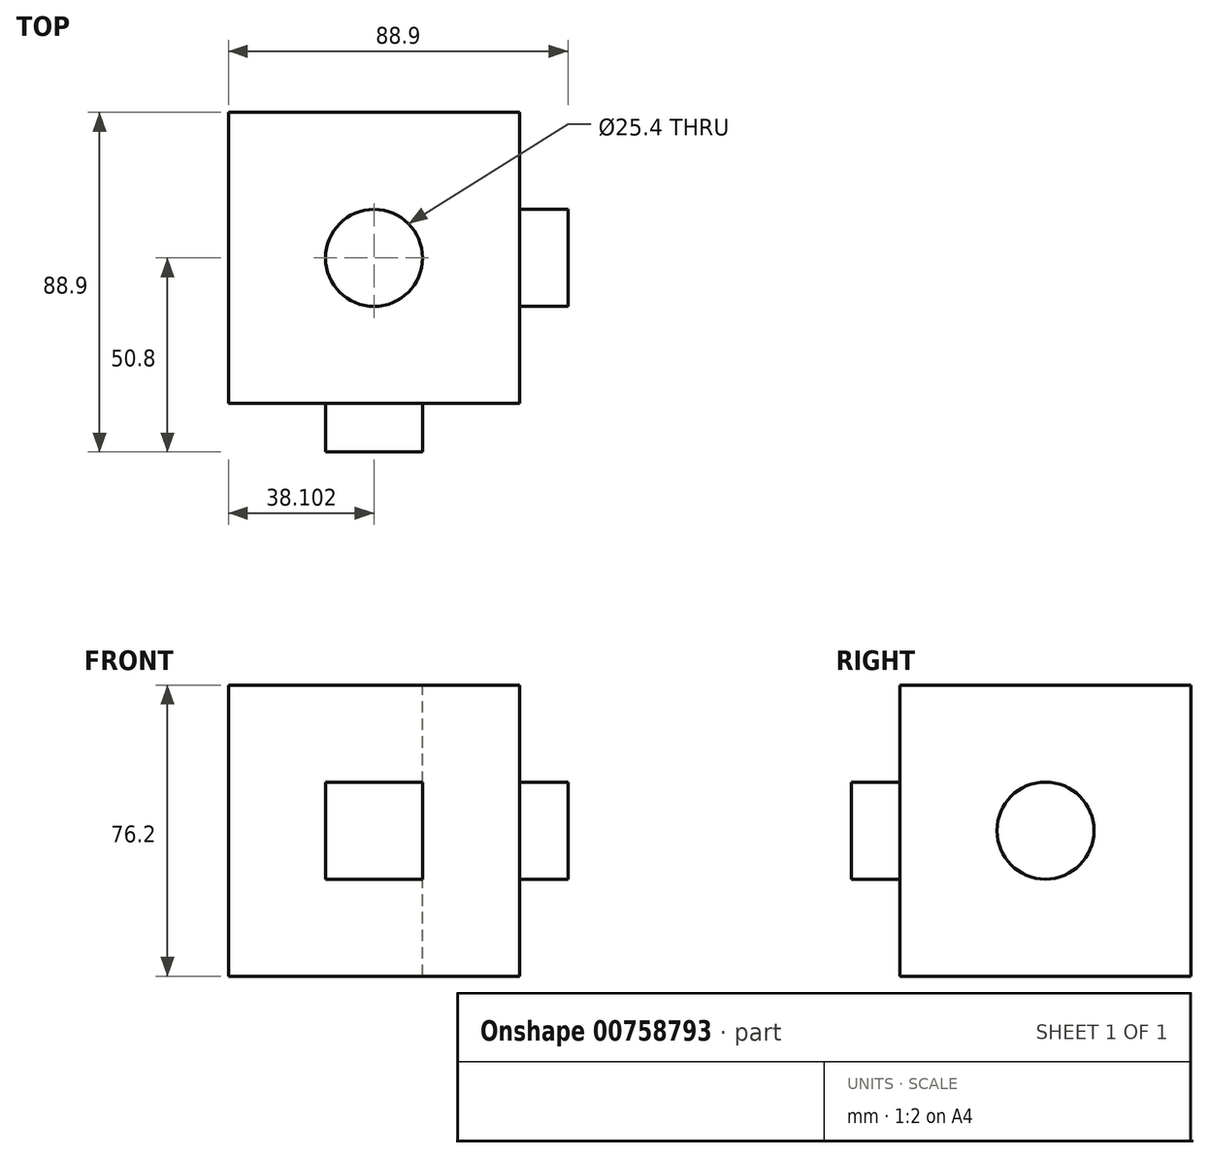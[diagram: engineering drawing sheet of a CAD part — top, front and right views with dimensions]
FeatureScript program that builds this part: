
annotation { "Feature Type Name" : "Feature", "Feature Type Description" : "" }
export const myFeature = defineFeature(function(context is Context, id is Id, definition is map)
    precondition{}
    {
        {
            var Q0;
            Q0=qCreatedBy(makeId("Front.planeOp"),FACE);
            var sketch = newSketch(context, id + "F0", { "sketchPlane" : qUnion([Q0])});
            skLineSegment(sketch, "E0.bottom", {"start": v(-35.84, 57.66) * mm, "end": v(40.36, 57.66) * mm});
            skLineSegment(sketch, "E0.top", {"start": v(-35.84, -18.54) * mm, "end": v(40.36, -18.54) * mm});
            skLineSegment(sketch, "E0.left", {"start": v(-35.84, 57.66) * mm, "end": v(-35.84, -18.54) * mm});
            skLineSegment(sketch, "E0.right", {"start": v(40.36, 57.66) * mm, "end": v(40.36, -18.54) * mm});
            skSolve(sketch);
        }
        {
            var Q0;
            Q0=makeQuery(id+"F0.imprint","IMPRINT",FACE,{"disambiguationData":[TD([[makeQuery(id+"F0.imprint","IMPRINT",EDGE,{"derivedFrom":sQuery(id+"F0.wireOp",EDGE,"E0.bottom")}),-1.0]])]});
            extrude(context, id + "F1", {"entities" : qUnion([Q0]), "depth" : 76.2 * mm, "offsetDistance" : 25.4 * mm});
        }
        {
            var Q0;
            Q0=makeQuery(id+"F1.opExtrude","CAP_FACE",FACE,{"disambiguationData":[OSD([sQuery(id+"F0.wireOp",EDGE,"E0.bottom"),sQuery(id+"F0.wireOp",EDGE,"E0.top"),sQuery(id+"F0.wireOp",EDGE,"E0.left"),sQuery(id+"F0.wireOp",EDGE,"E0.right")])],"isStart":false});
            var sketch = newSketch(context, id + "F2", { "sketchPlane" : qUnion([Q0])});
            skLineSegment(sketch, "E1.bottom", {"start": v(-10.44, 32.26) * mm, "end": v(14.96, 32.26) * mm});
            skLineSegment(sketch, "E1.top", {"start": v(-10.44, 6.86) * mm, "end": v(14.96, 6.86) * mm});
            skLineSegment(sketch, "E1.left", {"start": v(-10.44, 32.26) * mm, "end": v(-10.44, 6.86) * mm});
            skLineSegment(sketch, "E1.right", {"start": v(14.96, 32.26) * mm, "end": v(14.96, 6.86) * mm});
            skLineSegment(sketch, "E2.bottom", {"start": v(81.79, 20.03) * mm, "end": v(82.6, 20.03) * mm});
            skLineSegment(sketch, "E2.top", {"start": v(81.79, 20.2) * mm, "end": v(82.6, 20.2) * mm});
            skLineSegment(sketch, "E2.left", {"start": v(81.79, 20.03) * mm, "end": v(81.79, 20.2) * mm});
            skLineSegment(sketch, "E2.right", {"start": v(82.6, 20.03) * mm, "end": v(82.6, 20.2) * mm});
            skLineSegment(sketch, "E3.bottom", {"start": v(82.6, 20.03) * mm, "end": v(81.79, 20.03) * mm});
            skLineSegment(sketch, "E3.top", {"start": v(82.6, 20.03) * mm, "end": v(81.79, 20.03) * mm});
            skLineSegment(sketch, "E3.left", {"start": v(82.6, 20.03) * mm, "end": v(82.6, 20.03) * mm});
            skLineSegment(sketch, "E3.right", {"start": v(81.79, 20.03) * mm, "end": v(81.79, 20.03) * mm});
            skSolve(sketch);
        }
        {
            var Q0;
            Q0=makeQuery(id+"F2.imprint","IMPRINT",FACE,{"disambiguationData":[TD([[makeQuery(id+"F2.imprint","IMPRINT",EDGE,{"derivedFrom":sQuery(id+"F2.wireOp",EDGE,"E1.bottom")}),-1.0]])]});
            extrude(context, id + "F3", {"entities" : qUnion([Q0]), "operationType" : NewBodyOperationType.ADD, "depth" : 12.7 * mm, "offsetDistance" : 25.4 * mm});
        }
        {
            var Q0;
            Q0=makeQuery(id+"F1.opExtrude","SWEPT_FACE",FACE,{"disambiguationData":[OSD([sQuery(id+"F0.wireOp",EDGE,"E0.right")])]});
            var sketch = newSketch(context, id + "F4", { "sketchPlane" : qUnion([Q0])});
            skCircle(sketch, "E4", {"center": v(-38.1, 19.56) * mm, "radius": 12.7 * mm});
            skSolve(sketch);
        }
        {
            var Q0;
            Q0=makeQuery(id+"F4.imprint","IMPRINT",FACE,{"disambiguationData":[TD([[makeQuery(id+"F4.imprint","IMPRINT",EDGE,{"derivedFrom":sQuery(id+"F4.wireOp",EDGE,"E4")}),1.0]])]});
            extrude(context, id + "F5", {"entities" : qUnion([Q0]), "operationType" : NewBodyOperationType.ADD, "depth" : 12.7 * mm, "offsetDistance" : 25.4 * mm});
        }
        {
            var Q0;
            Q0=makeQuery(id+"F1.opExtrude","SWEPT_FACE",FACE,{"disambiguationData":[OSD([sQuery(id+"F0.wireOp",EDGE,"E0.bottom")])]});
            var sketch = newSketch(context, id + "F6", { "sketchPlane" : qUnion([Q0])});
            skPoint(sketch, "E5", {"position": v(2.26, -38.1) * mm});
            skSolve(sketch);
        }
        {
            var Q0;
            Q0=sQuery(id+"F6.wireOp",VERTEX,"E5");
            var Q1;
            Q1=makeQuery(id+"F1.opExtrude","SWEPT_BODY",BODY,{"disambiguationData":[OSD([sQuery(id+"F0.wireOp",EDGE,"E0.bottom"),sQuery(id+"F0.wireOp",EDGE,"E0.top"),sQuery(id+"F0.wireOp",EDGE,"E0.left"),sQuery(id+"F0.wireOp",EDGE,"E0.right")])]});
            hole(context, id + "F7", {"style" : HoleStyle.SIMPLE, "endStyle" : HoleEndStyle.THROUGH, "holeDiameter" : 25.4 * mm, "majorDiameter" : 6.35 * mm, "isTappedThrough" : true, "tappedDepth" : 12.7 * mm, "tapClearance" : 3, "locations" : qUnion([Q0]), "scope" : qUnion([Q1])});
        }
    });
